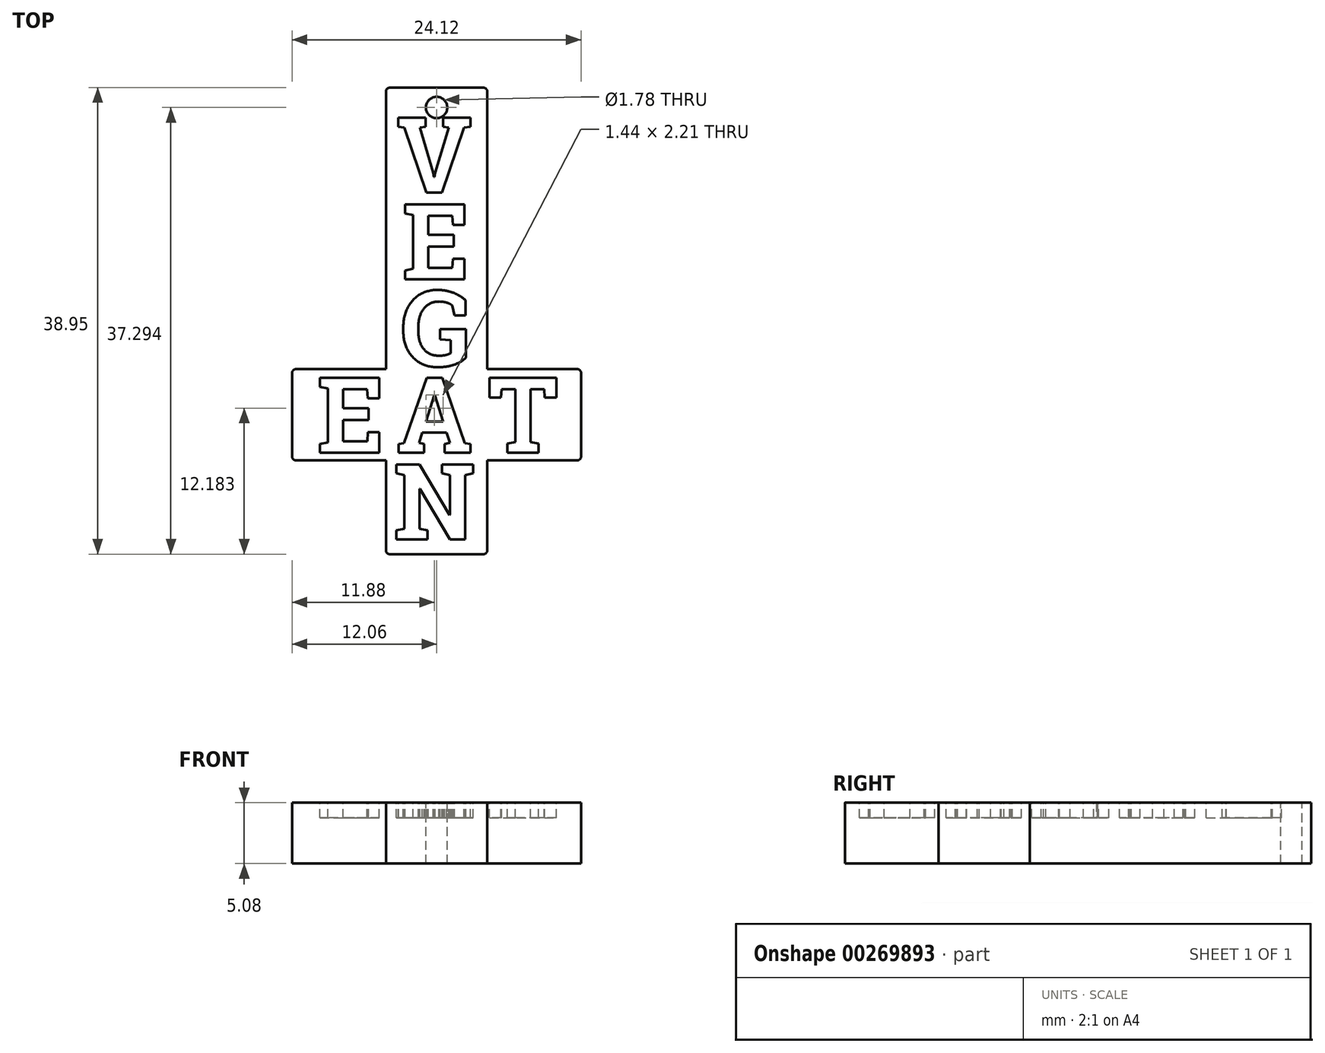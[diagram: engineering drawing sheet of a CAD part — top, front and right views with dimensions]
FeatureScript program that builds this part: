
annotation { "Feature Type Name" : "Feature", "Feature Type Description" : "" }
export const myFeature = defineFeature(function(context is Context, id is Id, definition is map)
    precondition{}
    {
        {
            var Q0;
            Q0=qCreatedBy(makeId("Top.planeOp"),FACE);
            cPlane(context, id + "F0", {"entities" : qUnion([Q0]), "cplaneType" : CPlaneType.OFFSET, "offset" : 5.08 * mm, "width" : 152.4 * mm, "height" : 152.4 * mm});
        }
        {
            var Q0;
            Q0=qCreatedBy(id+"F0.planeOp",FACE);
            var sketch = newSketch(context, id + "F1", { "sketchPlane" : qUnion([Q0])});
            skText(sketch, "E0", { "text": "G", "fontName": "RobotoSlab-Bold.ttf"});
            skText(sketch, "E1", { "text": "E", "fontName": "RobotoSlab-Bold.ttf"});
            skText(sketch, "E2", { "text": "V", "fontName": "RobotoSlab-Bold.ttf"});
            skText(sketch, "E3", { "text": "N", "fontName": "RobotoSlab-Bold.ttf"});
            skText(sketch, "E4", { "text": "A", "fontName": "RobotoSlab-Bold.ttf"});
            skText(sketch, "E5", { "text": "E", "fontName": "RobotoSlab-Bold.ttf"});
            skText(sketch, "E6", { "text": "T", "fontName": "RobotoSlab-Bold.ttf"});
            skPoint(sketch, "E7", {"position": v(-3.35, 0) * mm});
            skPoint(sketch, "E8", {"position": v(3.35, 0) * mm});
            skLineSegment(sketch, "E9", {"start": v(-3.35, 0) * mm, "end": v(3.35, 0) * mm, "construction": true});
            const initialGuessF1  = {"E0": [-0.00299, 0.00406, 1, 0, 0.00635], "E1": [-0.00287, 0.0113, 1, 0, 0.00635], "E2": [-0.00336, 0.01854, 1, 0, 0.00635], "E3": [-0.0036, -0.01041, 1, 0, 0.00635], "E4": [-0.00335, -0.00318, 1, 0, 0.00635], "E5": [-0.00998, -0.00318, 1, 0, 0.00635], "E6": [0.00424, -0.00317, 1, 0, 0.00635]};
            skSetInitialGuess(sketch, initialGuessF1);
            skSolve(sketch);
        }
        {
            var Q0;
            Q0=qCreatedBy(id+"F0.planeOp",FACE);
            var sketch = newSketch(context, id + "F2", { "sketchPlane" : qUnion([Q0])});
            skLineSegment(sketch, "E10.0", {"start": v(-3.36, 18.54) * mm, "end": v(-3.36, 24.9) * mm, "construction": true});
            skLineSegment(sketch, "E10.1", {"start": v(3.36, 18.54) * mm, "end": v(3.36, 24.9) * mm, "construction": true});
            skLineSegment(sketch, "E11.0", {"start": v(-3.6, -10.41) * mm, "end": v(-3.6, -4.06) * mm, "construction": true});
            skLineSegment(sketch, "E11.1", {"start": v(3.6, -10.41) * mm, "end": v(3.6, -4.06) * mm, "construction": true});
            skLineSegment(sketch, "E12.0", {"start": v(-3.6, -10.41) * mm, "end": v(3.6, -10.41) * mm, "construction": true});
            skLineSegment(sketch, "E13.0", {"start": v(-3.36, 24.9) * mm, "end": v(3.36, 24.9) * mm, "construction": true});
            skLineSegment(sketch, "E14.0", {"start": v(10.54, -3.18) * mm, "end": v(10.54, 3.17) * mm, "construction": true});
            skLineSegment(sketch, "E14.1", {"start": v(4.24, -3.17) * mm, "end": v(10.54, -3.18) * mm, "construction": true});
            skLineSegment(sketch, "E15.0", {"start": v(4.24, 3.17) * mm, "end": v(10.54, 3.17) * mm, "construction": true});
            skLineSegment(sketch, "E16.0", {"start": v(-9.98, -3.18) * mm, "end": v(-9.98, 3.17) * mm, "construction": true});
            skLineSegment(sketch, "E16.1", {"start": v(-9.98, -3.18) * mm, "end": v(-4.24, -3.17) * mm, "construction": true});
            skLineSegment(sketch, "E16.2", {"start": v(-9.98, 3.17) * mm, "end": v(-4.24, 3.18) * mm, "construction": true});
            skLineSegment(sketch, "E17.0", {"start": v(4.23, 3.81) * mm, "end": v(12.06, 3.8) * mm});
            skLineSegment(sketch, "E18.0", {"start": v(4.23, -3.81) * mm, "end": v(12.06, -3.81) * mm});
            skLineSegment(sketch, "E19.0", {"start": v(-12.06, -3.81) * mm, "end": v(-4.23, -3.81) * mm});
            skLineSegment(sketch, "E20.0", {"start": v(-12.06, 3.8) * mm, "end": v(-4.23, 3.81) * mm});
            skLineSegment(sketch, "E21.0", {"start": v(4.23, -11.64) * mm, "end": v(4.23, -3.81) * mm});
            skLineSegment(sketch, "E22.0", {"start": v(-4.23, -11.64) * mm, "end": v(-4.23, -3.81) * mm});
            skLineSegment(sketch, "E23.trimOffspring", {"start": v(4.23, 3.81) * mm, "end": v(4.23, 27.3) * mm});
            skLineSegment(sketch, "E24.trimOffspring", {"start": v(-4.23, 3.81) * mm, "end": v(-4.23, 27.3) * mm});
            skLineSegment(sketch, "E25", {"start": v(12.06, -3.81) * mm, "end": v(12.06, 3.81) * mm});
            skLineSegment(sketch, "E26", {"start": v(-12.06, -3.81) * mm, "end": v(-12.06, 3.8) * mm});
            skLineSegment(sketch, "E27", {"start": v(-4.23, -11.64) * mm, "end": v(4.23, -11.64) * mm});
            skLineSegment(sketch, "E28", {"start": v(-4.23, 27.3) * mm, "end": v(4.23, 27.3) * mm});
            skCircle(sketch, "E29", {"center": v(0, 25.65) * mm, "radius": 0.89 * mm});
            skLineSegment(sketch, "E30", {"start": v(0, 25.65) * mm, "end": v(0, 27.3) * mm, "construction": true});
            skSolve(sketch);
        }
        {
            var Q0;
            Q0 = qSketchRegion(id + "F2", true);
            var Q1;
            Q1=qCreatedBy(makeId("Top.planeOp"),FACE);
            extrude(context, id + "F3", {"entities" : qUnion([Q0]), "endBound" : BoundingType.UP_TO_SURFACE, "oppositeDirection" : true, "endBoundEntityFace" : qUnion([Q1]), "depth" : 25.4 * mm});
        }
        {
            var Q0;
            Q0 = qSketchRegion(id + "F1", true);
            extrude(context, id + "F4", {"entities" : qUnion([Q0]), "oppositeDirection" : true, "depth" : 1.27 * mm});
        }
        {
            var Q0;
            Q0=makeQuery(id+"F4.opExtrude","SWEPT_BODY",BODY,{"disambiguationData":[OSD([sQuery(id+"F1.wireOp",EDGE,"E0.sketch_text.stroke-0"),sQuery(id+"F1.wireOp",EDGE,"E0.sketch_text.stroke-1"),sQuery(id+"F1.wireOp",EDGE,"E0.sketch_text.stroke-2"),sQuery(id+"F1.wireOp",EDGE,"E0.sketch_text.stroke-3"),sQuery(id+"F1.wireOp",EDGE,"E0.sketch_text.stroke-4"),sQuery(id+"F1.wireOp",EDGE,"E0.sketch_text.stroke-5"),sQuery(id+"F1.wireOp",EDGE,"E0.sketch_text.stroke-6"),sQuery(id+"F1.wireOp",EDGE,"E0.sketch_text.stroke-7"),sQuery(id+"F1.wireOp",EDGE,"E0.sketch_text.stroke-8"),sQuery(id+"F1.wireOp",EDGE,"E0.sketch_text.stroke-9"),sQuery(id+"F1.wireOp",EDGE,"E0.sketch_text.stroke-10"),sQuery(id+"F1.wireOp",EDGE,"E0.sketch_text.stroke-11"),sQuery(id+"F1.wireOp",EDGE,"E0.sketch_text.stroke-12"),sQuery(id+"F1.wireOp",EDGE,"E0.sketch_text.stroke-13"),sQuery(id+"F1.wireOp",EDGE,"E0.sketch_text.stroke-14"),sQuery(id+"F1.wireOp",EDGE,"E0.sketch_text.stroke-15"),sQuery(id+"F1.wireOp",EDGE,"E0.sketch_text.stroke-16"),sQuery(id+"F1.wireOp",EDGE,"E0.sketch_text.stroke-17"),sQuery(id+"F1.wireOp",EDGE,"E0.sketch_text.stroke-18"),sQuery(id+"F1.wireOp",EDGE,"E0.sketch_text.stroke-19"),sQuery(id+"F1.wireOp",EDGE,"E0.sketch_text.stroke-20"),sQuery(id+"F1.wireOp",EDGE,"E0.sketch_text.stroke-21"),sQuery(id+"F1.wireOp",EDGE,"E0.sketch_text.stroke-22"),sQuery(id+"F1.wireOp",EDGE,"E0.sketch_text.stroke-23"),sQuery(id+"F1.wireOp",EDGE,"E0.sketch_text.stroke-24"),sQuery(id+"F1.wireOp",EDGE,"E0.sketch_text.stroke-25")])]});
            var Q1;
            Q1=makeQuery(id+"F4.opExtrude","SWEPT_BODY",BODY,{"disambiguationData":[OSD([sQuery(id+"F1.wireOp",EDGE,"E1.sketch_text.stroke-0"),sQuery(id+"F1.wireOp",EDGE,"E1.sketch_text.stroke-1"),sQuery(id+"F1.wireOp",EDGE,"E1.sketch_text.stroke-2"),sQuery(id+"F1.wireOp",EDGE,"E1.sketch_text.stroke-3"),sQuery(id+"F1.wireOp",EDGE,"E1.sketch_text.stroke-4"),sQuery(id+"F1.wireOp",EDGE,"E1.sketch_text.stroke-5"),sQuery(id+"F1.wireOp",EDGE,"E1.sketch_text.stroke-6"),sQuery(id+"F1.wireOp",EDGE,"E1.sketch_text.stroke-7"),sQuery(id+"F1.wireOp",EDGE,"E1.sketch_text.stroke-8"),sQuery(id+"F1.wireOp",EDGE,"E1.sketch_text.stroke-9"),sQuery(id+"F1.wireOp",EDGE,"E1.sketch_text.stroke-10"),sQuery(id+"F1.wireOp",EDGE,"E1.sketch_text.stroke-11"),sQuery(id+"F1.wireOp",EDGE,"E1.sketch_text.stroke-12"),sQuery(id+"F1.wireOp",EDGE,"E1.sketch_text.stroke-13"),sQuery(id+"F1.wireOp",EDGE,"E1.sketch_text.stroke-14"),sQuery(id+"F1.wireOp",EDGE,"E1.sketch_text.stroke-15"),sQuery(id+"F1.wireOp",EDGE,"E1.sketch_text.stroke-16"),sQuery(id+"F1.wireOp",EDGE,"E1.sketch_text.stroke-17"),sQuery(id+"F1.wireOp",EDGE,"E1.sketch_text.stroke-18"),sQuery(id+"F1.wireOp",EDGE,"E1.sketch_text.stroke-19"),sQuery(id+"F1.wireOp",EDGE,"E1.sketch_text.stroke-20")])]});
            var Q2;
            Q2=makeQuery(id+"F4.opExtrude","SWEPT_BODY",BODY,{"disambiguationData":[OSD([sQuery(id+"F1.wireOp",EDGE,"E2.sketch_text.stroke-0"),sQuery(id+"F1.wireOp",EDGE,"E2.sketch_text.stroke-1"),sQuery(id+"F1.wireOp",EDGE,"E2.sketch_text.stroke-2"),sQuery(id+"F1.wireOp",EDGE,"E2.sketch_text.stroke-3"),sQuery(id+"F1.wireOp",EDGE,"E2.sketch_text.stroke-4"),sQuery(id+"F1.wireOp",EDGE,"E2.sketch_text.stroke-5"),sQuery(id+"F1.wireOp",EDGE,"E2.sketch_text.stroke-6"),sQuery(id+"F1.wireOp",EDGE,"E2.sketch_text.stroke-7"),sQuery(id+"F1.wireOp",EDGE,"E2.sketch_text.stroke-8"),sQuery(id+"F1.wireOp",EDGE,"E2.sketch_text.stroke-9"),sQuery(id+"F1.wireOp",EDGE,"E2.sketch_text.stroke-10"),sQuery(id+"F1.wireOp",EDGE,"E2.sketch_text.stroke-11"),sQuery(id+"F1.wireOp",EDGE,"E2.sketch_text.stroke-12"),sQuery(id+"F1.wireOp",EDGE,"E2.sketch_text.stroke-13"),sQuery(id+"F1.wireOp",EDGE,"E2.sketch_text.stroke-14"),sQuery(id+"F1.wireOp",EDGE,"E2.sketch_text.stroke-15"),sQuery(id+"F1.wireOp",EDGE,"E2.sketch_text.stroke-16"),sQuery(id+"F1.wireOp",EDGE,"E2.sketch_text.stroke-17")])]});
            var Q3;
            Q3=makeQuery(id+"F4.opExtrude","SWEPT_BODY",BODY,{"disambiguationData":[OSD([sQuery(id+"F1.wireOp",EDGE,"E3.sketch_text.stroke-0"),sQuery(id+"F1.wireOp",EDGE,"E3.sketch_text.stroke-1"),sQuery(id+"F1.wireOp",EDGE,"E3.sketch_text.stroke-2"),sQuery(id+"F1.wireOp",EDGE,"E3.sketch_text.stroke-3"),sQuery(id+"F1.wireOp",EDGE,"E3.sketch_text.stroke-4"),sQuery(id+"F1.wireOp",EDGE,"E3.sketch_text.stroke-5"),sQuery(id+"F1.wireOp",EDGE,"E3.sketch_text.stroke-6"),sQuery(id+"F1.wireOp",EDGE,"E3.sketch_text.stroke-7"),sQuery(id+"F1.wireOp",EDGE,"E3.sketch_text.stroke-8"),sQuery(id+"F1.wireOp",EDGE,"E3.sketch_text.stroke-9"),sQuery(id+"F1.wireOp",EDGE,"E3.sketch_text.stroke-10"),sQuery(id+"F1.wireOp",EDGE,"E3.sketch_text.stroke-11"),sQuery(id+"F1.wireOp",EDGE,"E3.sketch_text.stroke-12"),sQuery(id+"F1.wireOp",EDGE,"E3.sketch_text.stroke-13"),sQuery(id+"F1.wireOp",EDGE,"E3.sketch_text.stroke-14"),sQuery(id+"F1.wireOp",EDGE,"E3.sketch_text.stroke-15"),sQuery(id+"F1.wireOp",EDGE,"E3.sketch_text.stroke-16"),sQuery(id+"F1.wireOp",EDGE,"E3.sketch_text.stroke-17"),sQuery(id+"F1.wireOp",EDGE,"E3.sketch_text.stroke-18"),sQuery(id+"F1.wireOp",EDGE,"E3.sketch_text.stroke-19"),sQuery(id+"F1.wireOp",EDGE,"E3.sketch_text.stroke-20"),sQuery(id+"F1.wireOp",EDGE,"E3.sketch_text.stroke-21"),sQuery(id+"F1.wireOp",EDGE,"E3.sketch_text.stroke-22"),sQuery(id+"F1.wireOp",EDGE,"E3.sketch_text.stroke-23")])]});
            var Q4;
            Q4=makeQuery(id+"F4.opExtrude","SWEPT_BODY",BODY,{"disambiguationData":[OSD([sQuery(id+"F1.wireOp",EDGE,"E4.sketch_text.stroke-0"),sQuery(id+"F1.wireOp",EDGE,"E4.sketch_text.stroke-1"),sQuery(id+"F1.wireOp",EDGE,"E4.sketch_text.stroke-2"),sQuery(id+"F1.wireOp",EDGE,"E4.sketch_text.stroke-3"),sQuery(id+"F1.wireOp",EDGE,"E4.sketch_text.stroke-4"),sQuery(id+"F1.wireOp",EDGE,"E4.sketch_text.stroke-5"),sQuery(id+"F1.wireOp",EDGE,"E4.sketch_text.stroke-6"),sQuery(id+"F1.wireOp",EDGE,"E4.sketch_text.stroke-7"),sQuery(id+"F1.wireOp",EDGE,"E4.sketch_text.stroke-8"),sQuery(id+"F1.wireOp",EDGE,"E4.sketch_text.stroke-9"),sQuery(id+"F1.wireOp",EDGE,"E4.sketch_text.stroke-10"),sQuery(id+"F1.wireOp",EDGE,"E4.sketch_text.stroke-11"),sQuery(id+"F1.wireOp",EDGE,"E4.sketch_text.stroke-12"),sQuery(id+"F1.wireOp",EDGE,"E4.sketch_text.stroke-13"),sQuery(id+"F1.wireOp",EDGE,"E4.sketch_text.stroke-14"),sQuery(id+"F1.wireOp",EDGE,"E4.sketch_text.stroke-15"),sQuery(id+"F1.wireOp",EDGE,"E4.sketch_text.stroke-16"),sQuery(id+"F1.wireOp",EDGE,"E4.sketch_text.stroke-17"),sQuery(id+"F1.wireOp",EDGE,"E4.sketch_text.stroke-18"),sQuery(id+"F1.wireOp",EDGE,"E4.sketch_text.stroke-19")])]});
            var Q5;
            Q5=makeQuery(id+"F4.opExtrude","SWEPT_BODY",BODY,{"disambiguationData":[OSD([sQuery(id+"F1.wireOp",EDGE,"E5.sketch_text.stroke-0"),sQuery(id+"F1.wireOp",EDGE,"E5.sketch_text.stroke-1"),sQuery(id+"F1.wireOp",EDGE,"E5.sketch_text.stroke-2"),sQuery(id+"F1.wireOp",EDGE,"E5.sketch_text.stroke-3"),sQuery(id+"F1.wireOp",EDGE,"E5.sketch_text.stroke-4"),sQuery(id+"F1.wireOp",EDGE,"E5.sketch_text.stroke-5"),sQuery(id+"F1.wireOp",EDGE,"E5.sketch_text.stroke-6"),sQuery(id+"F1.wireOp",EDGE,"E5.sketch_text.stroke-7"),sQuery(id+"F1.wireOp",EDGE,"E5.sketch_text.stroke-8"),sQuery(id+"F1.wireOp",EDGE,"E5.sketch_text.stroke-9"),sQuery(id+"F1.wireOp",EDGE,"E5.sketch_text.stroke-10"),sQuery(id+"F1.wireOp",EDGE,"E5.sketch_text.stroke-11"),sQuery(id+"F1.wireOp",EDGE,"E5.sketch_text.stroke-12"),sQuery(id+"F1.wireOp",EDGE,"E5.sketch_text.stroke-13"),sQuery(id+"F1.wireOp",EDGE,"E5.sketch_text.stroke-14"),sQuery(id+"F1.wireOp",EDGE,"E5.sketch_text.stroke-15"),sQuery(id+"F1.wireOp",EDGE,"E5.sketch_text.stroke-16"),sQuery(id+"F1.wireOp",EDGE,"E5.sketch_text.stroke-17"),sQuery(id+"F1.wireOp",EDGE,"E5.sketch_text.stroke-18"),sQuery(id+"F1.wireOp",EDGE,"E5.sketch_text.stroke-19"),sQuery(id+"F1.wireOp",EDGE,"E5.sketch_text.stroke-20")])]});
            var Q6;
            Q6=makeQuery(id+"F4.opExtrude","SWEPT_BODY",BODY,{"disambiguationData":[OSD([sQuery(id+"F1.wireOp",EDGE,"E6.sketch_text.stroke-0"),sQuery(id+"F1.wireOp",EDGE,"E6.sketch_text.stroke-1"),sQuery(id+"F1.wireOp",EDGE,"E6.sketch_text.stroke-2"),sQuery(id+"F1.wireOp",EDGE,"E6.sketch_text.stroke-3"),sQuery(id+"F1.wireOp",EDGE,"E6.sketch_text.stroke-4"),sQuery(id+"F1.wireOp",EDGE,"E6.sketch_text.stroke-5"),sQuery(id+"F1.wireOp",EDGE,"E6.sketch_text.stroke-6"),sQuery(id+"F1.wireOp",EDGE,"E6.sketch_text.stroke-7"),sQuery(id+"F1.wireOp",EDGE,"E6.sketch_text.stroke-8"),sQuery(id+"F1.wireOp",EDGE,"E6.sketch_text.stroke-9"),sQuery(id+"F1.wireOp",EDGE,"E6.sketch_text.stroke-10"),sQuery(id+"F1.wireOp",EDGE,"E6.sketch_text.stroke-11"),sQuery(id+"F1.wireOp",EDGE,"E6.sketch_text.stroke-12"),sQuery(id+"F1.wireOp",EDGE,"E6.sketch_text.stroke-13"),sQuery(id+"F1.wireOp",EDGE,"E6.sketch_text.stroke-14"),sQuery(id+"F1.wireOp",EDGE,"E6.sketch_text.stroke-15")])]});
            var Q7;
            Q7=makeQuery(id+"F3.opExtrude","SWEPT_BODY",BODY,{"disambiguationData":[OSD([sQuery(id+"F2.wireOp",EDGE,"E17.0"),sQuery(id+"F2.wireOp",EDGE,"E18.0"),sQuery(id+"F2.wireOp",EDGE,"E19.0"),sQuery(id+"F2.wireOp",EDGE,"E20.0"),sQuery(id+"F2.wireOp",EDGE,"E21.0"),sQuery(id+"F2.wireOp",EDGE,"E22.0"),sQuery(id+"F2.wireOp",EDGE,"E23.trimOffspring"),sQuery(id+"F2.wireOp",EDGE,"E24.trimOffspring"),sQuery(id+"F2.wireOp",EDGE,"E25"),sQuery(id+"F2.wireOp",EDGE,"E26"),sQuery(id+"F2.wireOp",EDGE,"E27"),sQuery(id+"F2.wireOp",EDGE,"E28"),sQuery(id+"F2.wireOp",EDGE,"E29")])]});
            booleanBodies(context, id + "F5", {"operationType" : BooleanOperationType.SUBTRACTION, "tools" : qUnion([Q0, Q1, Q2, Q3, Q4, Q5, Q6]), "targets" : qUnion([Q7]), "keepTools" : true});
        }
        {
            var Q0;
            Q0=makeQuery(id+"F3.opExtrude","SWEPT_EDGE",EDGE,{"disambiguationData":[OSD([sQuery(id+"F2.wireOp",EDGE,"E24.trimOffspring"),sQuery(id+"F2.wireOp",EDGE,"E28")])]});
            var Q1;
            Q1=makeQuery(id+"F3.opExtrude","SWEPT_EDGE",EDGE,{"disambiguationData":[OSD([sQuery(id+"F2.wireOp",EDGE,"E23.trimOffspring"),sQuery(id+"F2.wireOp",EDGE,"E28")])]});
            var Q2;
            Q2=makeQuery(id+"F3.opExtrude","SWEPT_EDGE",EDGE,{"disambiguationData":[OSD([sQuery(id+"F2.wireOp",EDGE,"E20.0"),sQuery(id+"F2.wireOp",EDGE,"E26")])]});
            var Q3;
            Q3=makeQuery(id+"F3.opExtrude","SWEPT_EDGE",EDGE,{"disambiguationData":[OSD([sQuery(id+"F2.wireOp",EDGE,"E19.0"),sQuery(id+"F2.wireOp",EDGE,"E26")])]});
            var Q4;
            Q4=makeQuery(id+"F3.opExtrude","SWEPT_EDGE",EDGE,{"disambiguationData":[OSD([sQuery(id+"F2.wireOp",EDGE,"E22.0"),sQuery(id+"F2.wireOp",EDGE,"E27")])]});
            var Q5;
            Q5=makeQuery(id+"F3.opExtrude","SWEPT_EDGE",EDGE,{"disambiguationData":[OSD([sQuery(id+"F2.wireOp",EDGE,"E21.0"),sQuery(id+"F2.wireOp",EDGE,"E27")])]});
            var Q6;
            Q6=makeQuery(id+"F3.opExtrude","SWEPT_EDGE",EDGE,{"disambiguationData":[OSD([sQuery(id+"F2.wireOp",EDGE,"E18.0"),sQuery(id+"F2.wireOp",EDGE,"E25")])]});
            var Q7;
            Q7=makeQuery(id+"F3.opExtrude","SWEPT_EDGE",EDGE,{"disambiguationData":[OSD([sQuery(id+"F2.wireOp",EDGE,"E17.0"),sQuery(id+"F2.wireOp",EDGE,"E25")])]});
            fillet(context, id + "F6", {"entities" : qUnion([Q0, Q1, Q2, Q3, Q4, Q5, Q6, Q7]), "radius" : 0.32 * mm, "tangentPropagation" : true, "allowEdgeOverflow" : false});
        }
    });
